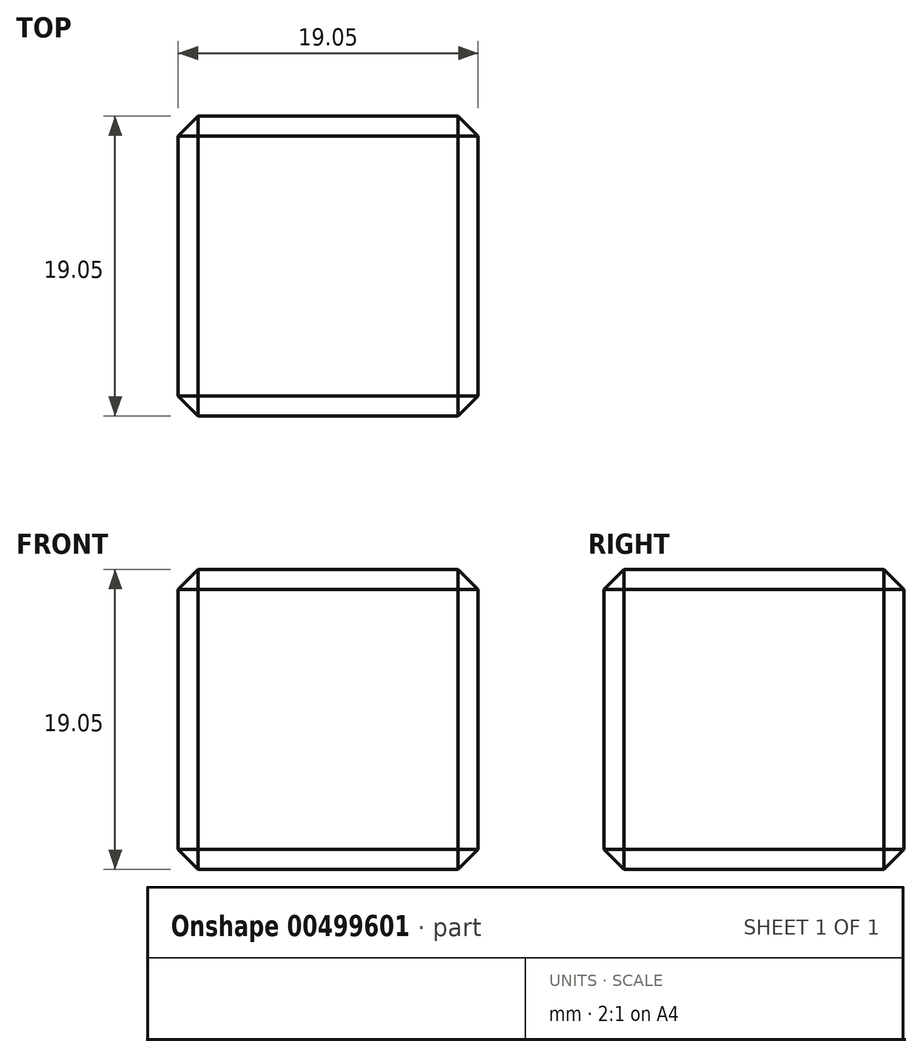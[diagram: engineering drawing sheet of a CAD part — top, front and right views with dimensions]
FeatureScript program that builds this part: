
annotation { "Feature Type Name" : "Feature", "Feature Type Description" : "" }
export const myFeature = defineFeature(function(context is Context, id is Id, definition is map)
    precondition{}
    {
        {
            var Q0;
            Q0=qCreatedBy(makeId("Top.planeOp"),FACE);
            var sketch = newSketch(context, id + "F0", { "sketchPlane" : qUnion([Q0])});
            skLineSegment(sketch, "E0.bottom", {"start": v(-11.3, -12.83) * mm, "end": v(7.76, -12.83) * mm});
            skLineSegment(sketch, "E0.top", {"start": v(-11.3, 6.22) * mm, "end": v(7.76, 6.22) * mm});
            skLineSegment(sketch, "E0.left", {"start": v(-11.3, -12.83) * mm, "end": v(-11.3, 6.22) * mm});
            skLineSegment(sketch, "E0.right", {"start": v(7.76, -12.83) * mm, "end": v(7.76, 6.22) * mm});
            skSolve(sketch);
        }
        {
            var Q0;
            Q0=makeQuery(id+"F0.imprint","IMPRINT",FACE,{"disambiguationData":[TD([[makeQuery(id+"F0.imprint","IMPRINT",EDGE,{"derivedFrom":sQuery(id+"F0.wireOp",EDGE,"E0.bottom")}),1.0]])]});
            extrude(context, id + "F1", {"entities" : qUnion([Q0]), "depth" : 19.05 * mm});
        }
        {
            var Q0;
            Q0=makeQuery(id+"F1.opExtrude","CAP_EDGE",EDGE,{"disambiguationData":[OSD([sQuery(id+"F0.wireOp",EDGE,"E0.left")])],"isStart":false});
            var Q1;
            Q1=makeQuery(id+"F1.opExtrude","CAP_EDGE",EDGE,{"disambiguationData":[OSD([sQuery(id+"F0.wireOp",EDGE,"E0.top")])],"isStart":false});
            var Q2;
            Q2=makeQuery(id+"F1.opExtrude","CAP_EDGE",EDGE,{"disambiguationData":[OSD([sQuery(id+"F0.wireOp",EDGE,"E0.bottom")])],"isStart":false});
            var Q3;
            Q3=makeQuery(id+"F1.opExtrude","CAP_EDGE",EDGE,{"disambiguationData":[OSD([sQuery(id+"F0.wireOp",EDGE,"E0.right")])],"isStart":false});
            var Q4;
            Q4=makeQuery(id+"F1.opExtrude","SWEPT_EDGE",EDGE,{"disambiguationData":[OSD([sQuery(id+"F0.wireOp",EDGE,"E0.bottom"),sQuery(id+"F0.wireOp",EDGE,"E0.right")])]});
            var Q5;
            Q5=makeQuery(id+"F1.opExtrude","CAP_EDGE",EDGE,{"disambiguationData":[OSD([sQuery(id+"F0.wireOp",EDGE,"E0.right")])],"isStart":true});
            var Q6;
            Q6=makeQuery(id+"F1.opExtrude","CAP_EDGE",EDGE,{"disambiguationData":[OSD([sQuery(id+"F0.wireOp",EDGE,"E0.bottom")])],"isStart":true});
            var Q7;
            Q7=makeQuery(id+"F1.opExtrude","CAP_EDGE",EDGE,{"disambiguationData":[OSD([sQuery(id+"F0.wireOp",EDGE,"E0.top")])],"isStart":true});
            var Q8;
            Q8=makeQuery(id+"F1.opExtrude","SWEPT_EDGE",EDGE,{"disambiguationData":[OSD([sQuery(id+"F0.wireOp",EDGE,"E0.top"),sQuery(id+"F0.wireOp",EDGE,"E0.left")])]});
            var Q9;
            Q9=makeQuery(id+"F1.opExtrude","SWEPT_EDGE",EDGE,{"disambiguationData":[OSD([sQuery(id+"F0.wireOp",EDGE,"E0.top"),sQuery(id+"F0.wireOp",EDGE,"E0.right")])]});
            var Q10;
            Q10=makeQuery(id+"F1.opExtrude","SWEPT_EDGE",EDGE,{"disambiguationData":[OSD([sQuery(id+"F0.wireOp",EDGE,"E0.bottom"),sQuery(id+"F0.wireOp",EDGE,"E0.left")])]});
            var Q11;
            Q11=makeQuery(id+"F1.opExtrude","CAP_EDGE",EDGE,{"disambiguationData":[OSD([sQuery(id+"F0.wireOp",EDGE,"E0.left")])],"isStart":true});
            chamfer(context, id + "F2", {"entities" : qUnion([Q0, Q1, Q2, Q3, Q4, Q5, Q6, Q7, Q8, Q9, Q10, Q11]), "width" : 1.27 * mm, "tangentPropagation" : true});
        }
    });
